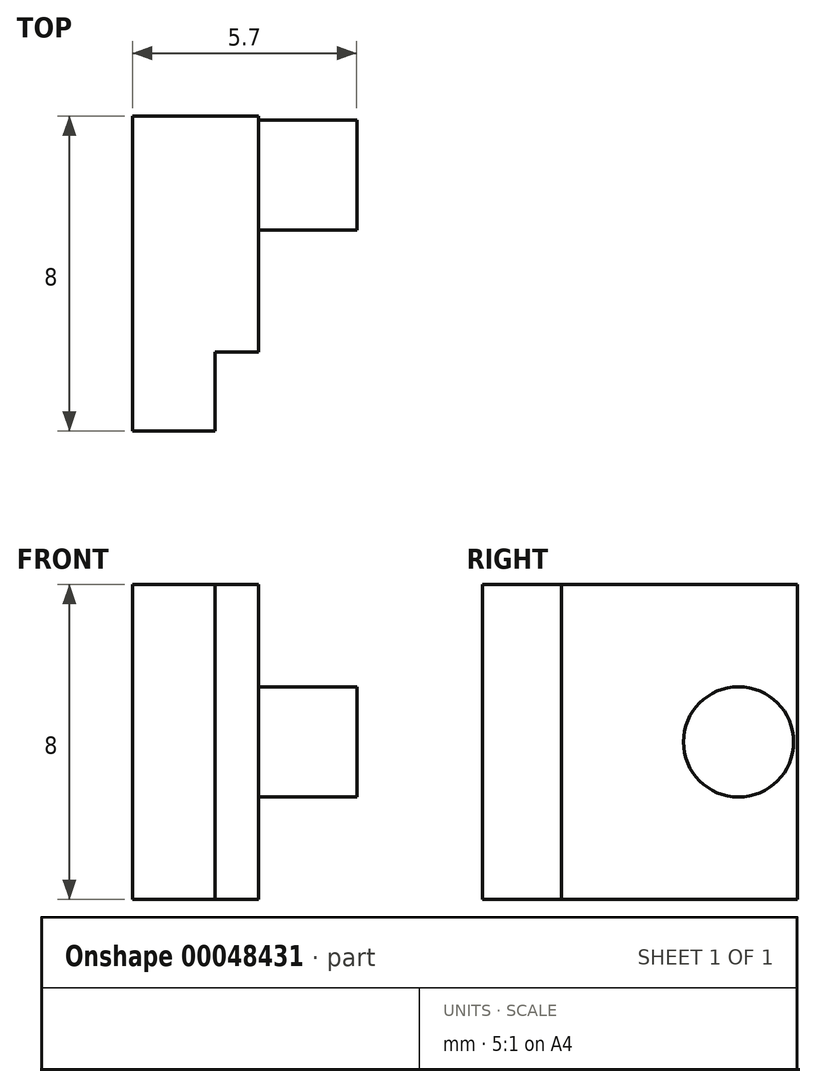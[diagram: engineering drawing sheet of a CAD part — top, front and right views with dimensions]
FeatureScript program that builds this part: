
annotation { "Feature Type Name" : "Feature", "Feature Type Description" : "" }
export const myFeature = defineFeature(function(context is Context, id is Id, definition is map)
    precondition{}
    {
        {
            var Q0;
            Q0=qCreatedBy(makeId("Top.planeOp"),FACE);
            var sketch = newSketch(context, id + "F0", { "sketchPlane" : qUnion([Q0])});
            skLineSegment(sketch, "E0", {"start": v(-34.34, 13.44) * mm, "end": v(-32.24, 13.44) * mm});
            skLineSegment(sketch, "E1", {"start": v(-34.34, 13.44) * mm, "end": v(-34.34, 21.44) * mm});
            skLineSegment(sketch, "E2", {"start": v(-32.24, 13.44) * mm, "end": v(-32.24, 15.44) * mm});
            skLineSegment(sketch, "E3", {"start": v(-34.34, 21.44) * mm, "end": v(-31.14, 21.44) * mm});
            skLineSegment(sketch, "E4", {"start": v(-32.24, 15.44) * mm, "end": v(-31.14, 15.44) * mm});
            skLineSegment(sketch, "E5", {"start": v(-31.14, 15.44) * mm, "end": v(-31.14, 21.44) * mm});
            skSolve(sketch);
        }
        {
            var Q0;
            Q0=makeQuery(id+"F0.imprint","IMPRINT",FACE,{"disambiguationData":[TD([[makeQuery(id+"F0.imprint","IMPRINT",EDGE,{"derivedFrom":sQuery(id+"F0.wireOp",EDGE,"E0")}),1.0]])]});
            extrude(context, id + "F1", {"entities" : qUnion([Q0]), "depth" : 8 * mm});
        }
        {
            var Q0;
            Q0=makeQuery(id+"F1.opExtrude","SWEPT_FACE",FACE,{"disambiguationData":[OSD([sQuery(id+"F0.wireOp",EDGE,"E5")])]});
            var sketch = newSketch(context, id + "F2", { "sketchPlane" : qUnion([Q0])});
            skCircle(sketch, "E6", {"center": v(19.94, 4) * mm, "radius": 1.4 * mm});
            skLineSegment(sketch, "E7", {"start": v(21.44, 4) * mm, "end": v(19.94, 4) * mm, "construction": true});
            skPoint(sketch, "E7.endSnap0", {"position": v(21.44, 4) * mm});
            skSolve(sketch);
        }
        {
            var Q0;
            Q0 = qSketchRegion(id + "F2", true);
            extrude(context, id + "F3", {"entities" : qUnion([Q0]), "operationType" : NewBodyOperationType.ADD, "depth" : 2.5 * mm});
        }
    });
